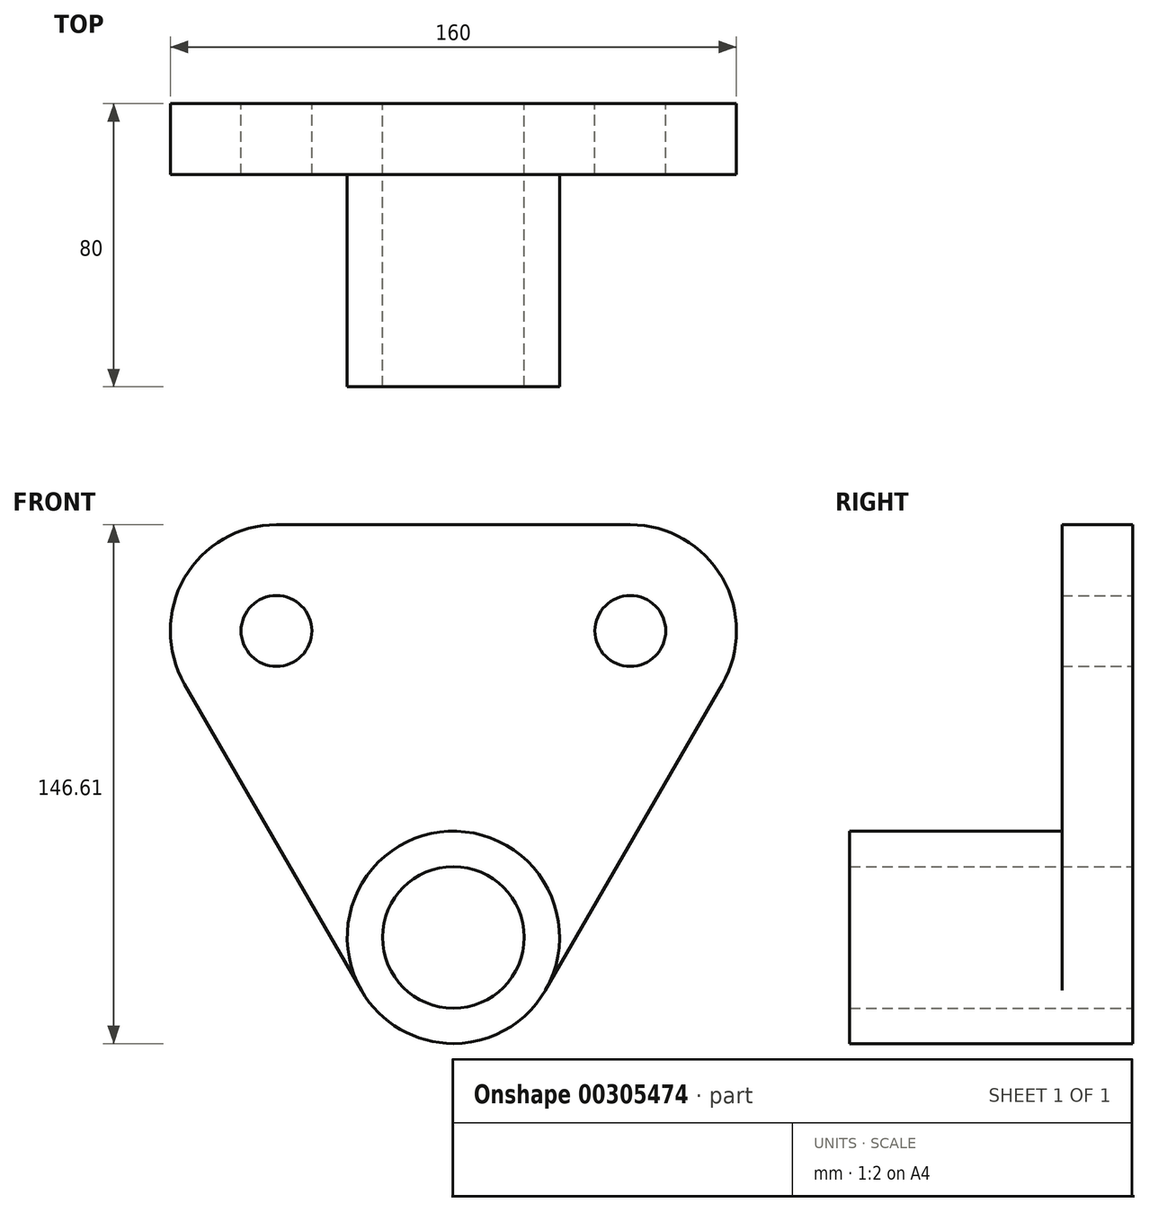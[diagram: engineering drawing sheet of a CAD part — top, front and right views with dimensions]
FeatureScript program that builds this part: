
annotation { "Feature Type Name" : "Feature", "Feature Type Description" : "" }
export const myFeature = defineFeature(function(context is Context, id is Id, definition is map)
    precondition{}
    {
        {
            var Q0;
            Q0=qCreatedBy(makeId("Front.planeOp"),FACE);
            var sketch = newSketch(context, id + "F0", { "sketchPlane" : qUnion([Q0])});
            skLineSegment(sketch, "E0", {"start": v(0, 71.03) * mm, "end": v(0, -75.48) * mm, "construction": true});
            skPoint(sketch, "E1.orphan", {"position": v(0, 43.8) * mm});
            skLineSegment(sketch, "E2.0", {"start": v(-50, 72.57) * mm, "end": v(-50, -75.48) * mm, "construction": true});
            skLineSegment(sketch, "E3.0", {"start": v(50, 72.57) * mm, "end": v(50, -75.48) * mm, "construction": true});
            skLineSegment(sketch, "E4", {"start": v(-60, 42.57) * mm, "end": v(91.22, 42.57) * mm, "construction": true});
            skCircle(sketch, "E5", {"center": v(-50, 42.57) * mm, "radius": 30 * mm});
            skCircle(sketch, "E6", {"center": v(-50, 42.57) * mm, "radius": 10 * mm});
            skCircle(sketch, "E7", {"center": v(50, 42.57) * mm, "radius": 30 * mm});
            skCircle(sketch, "E8", {"center": v(50, 42.57) * mm, "radius": 10 * mm});
            skLineSegment(sketch, "E9", {"start": v(-50, 72.57) * mm, "end": v(50, 72.57) * mm});
            skLineSegment(sketch, "E10", {"start": v(-50, 42.57) * mm, "end": v(0, -44.04) * mm, "construction": true});
            skLineSegment(sketch, "E11", {"start": v(0, -44.04) * mm, "end": v(50, 42.57) * mm, "construction": true});
            skCircle(sketch, "E12", {"center": v(0, -44.04) * mm, "radius": 30 * mm});
            skCircle(sketch, "E13", {"center": v(0, -44.04) * mm, "radius": 20 * mm});
            skLineSegment(sketch, "E14", {"start": v(-75.98, 27.57) * mm, "end": v(-25.98, -59.04) * mm});
            skLineSegment(sketch, "E15", {"start": v(75.98, 27.57) * mm, "end": v(25.98, -59.04) * mm});
            skSolve(sketch);
        }
        {
            var Q0;
            Q0 = qSketchRegion(id + "F0", true);
            extrude(context, id + "F1", {"entities" : qUnion([Q0]), "depth" : 20 * mm});
        }
        {
            var Q0;
            Q0=makeQuery(id+"F0.imprint","IMPRINT",FACE,{"disambiguationData":[TD([[makeQuery(id+"F0.imprint","IMPRINT",EDGE,{"derivedFrom":sQuery(id+"F0.wireOp",EDGE,"E13")}),-1.0]])]});
            extrude(context, id + "F2", {"entities" : qUnion([Q0]), "operationType" : NewBodyOperationType.ADD, "depth" : 80 * mm});
        }
    });
